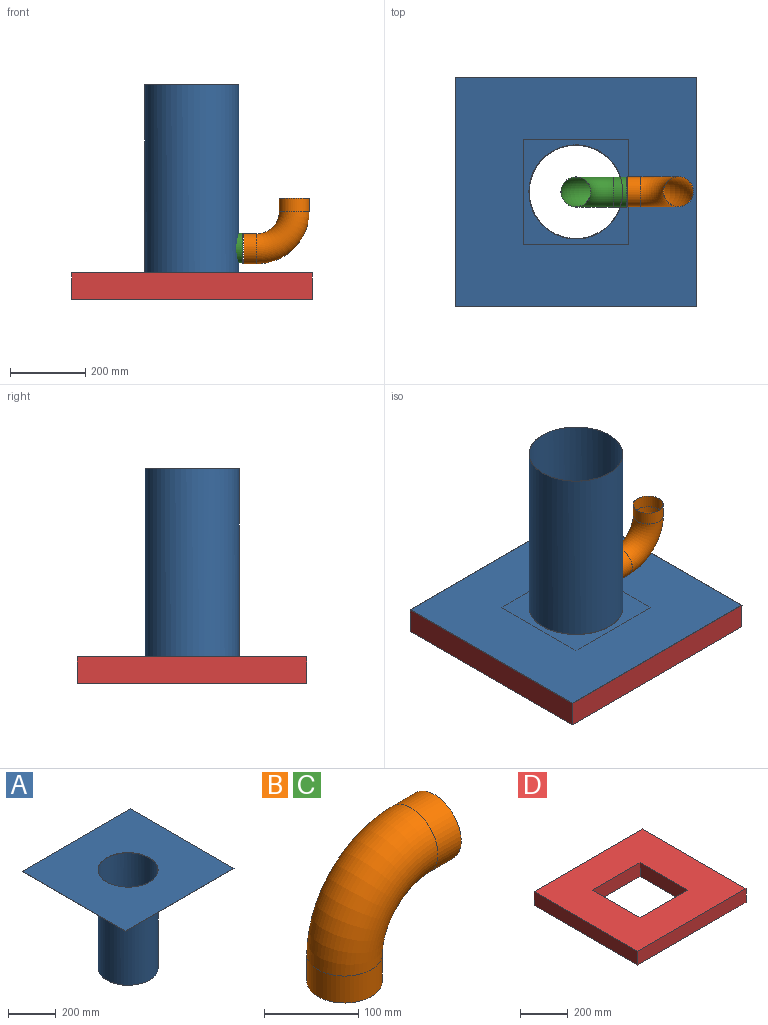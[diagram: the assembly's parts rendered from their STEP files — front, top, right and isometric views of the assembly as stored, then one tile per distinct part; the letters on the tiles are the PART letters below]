
ASSEMBLY  parts=4 mates=2
PART A: 12 faces, bbox 640x610x501 mm
  f0: plane 214.79x210.58mm, normal (0,0,1), area 124.6mm2, adj f1,f2,f8
  f1: cylinder r=124.5mm len=500mm, axis (0,0,-1), area 391128.3mm2, adj f0,f3,f11
  f2: cylinder r=125mm len=500mm, axis (0,0,-1), area 392699.1mm2, adj f0,f3,f4
  f3: plane 250x250mm, normal (0,0,-1), area 391.9mm2, adj f1,f2
  f4: plane 640x610mm, normal (0,0,-1), area 341312.6mm2, adj f2,f5,f6,f7,f8,f9
  f5: plane 610x1mm, normal (-1,0,0), area 610mm2, adj f4,f6,f9,f10
  f6: plane 640x1mm, normal (0,-1,0), area 640mm2, adj f4,f5,f7,f10
  f7: plane 610x1mm, normal (1,0,0), area 610mm2, adj f4,f6,f9,f10
  f8: cylinder r=124.5mm len=249mm, axis (0,0,-1), area 782.3mm2, adj f0,f4,f10,f11
  f9: plane 640x1mm, normal (0,1,0), area 640mm2, adj f4,f5,f7,f10
  f10: plane 640x610mm, normal (0,0,1), area 341704.5mm2, adj f5,f6,f7,f8,f9
  f11: plane 214.79x210.58mm, normal (0,0,-1), area 124.6mm2, adj f1,f8
PART B: 8 faces, bbox 186.5x80x186.5 mm
  f0: torus R=100mm, axis (0,-1,0), area 38984.9mm2, adj f2,f5
  f1: torus R=100mm, axis (0,-1,0), area 39478.4mm2, adj f3,f6
  f2: cylinder r=39.5mm len=79mm, axis (-1,0,0), area 8686.5mm2, adj f0,f4
  f3: cylinder r=40mm len=80mm, axis (-1,0,0), area 8796.5mm2, adj f1,f4
  f4: plane 80x80mm, normal (1,0,0), area 124.9mm2, adj f2,f3
  f5: cylinder r=39.5mm len=79mm, axis (0,0,1), area 8686.5mm2, adj f0,f7
  f6: cylinder r=40mm len=80mm, axis (0,0,1), area 8796.5mm2, adj f1,f7
  f7: plane 80x80mm, normal (0,0,-1), area 124.9mm2, adj f5,f6
PART C: same geometry as B
PART D: 10 faces, bbox 640x610x70 mm
  f0: plane 610x70mm, normal (-1,0,0), area 42700mm2, adj f1,f7,f8,f9
  f1: plane 640x70mm, normal (0,-1,0), area 44800mm2, adj f0,f2,f8,f9
  f2: plane 610x70mm, normal (1,0,0), area 42700mm2, adj f1,f7,f8,f9
  f3: plane 280x70mm, normal (0,1,0), area 19600mm2, adj f4,f6,f8,f9
  f4: plane 280x70mm, normal (1,0,0), area 19600mm2, adj f3,f5,f8,f9
  f5: plane 280x70mm, normal (0,-1,0), area 19600mm2, adj f4,f6,f8,f9
  f6: plane 280x70mm, normal (-1,0,0), area 19600mm2, adj f3,f5,f8,f9
  f7: plane 640x70mm, normal (0,1,0), area 44800mm2, adj f0,f2,f8,f9
  f8: plane 640x610mm, normal (0,0,1), area 312000mm2, adj f0,f1,f2,f3,f4,f5,f6,f7
  f9: plane 640x610mm, normal (0,0,-1), area 312000mm2, adj f0,f1,f2,f3,f4,f5,f6,f7
PLACE A rot(axis=(0,1,0),180deg) t=(-199.14,-74.24,659.28)mm
PLACE B rot(axis=(-0.71,0,-0.71),180deg) t=(31.24,105.56,-192.64)mm
PLACE C rot(axis=(0,-1,0),90deg) t=(98.24,-116.64,-190.73)mm
PLACE D t=(55.99,-73.89,18.28)mm fixed
MATE fastened C.f2 <-> A.f1  axis (0,0,-1) through (-71.76,-6.04,289.28)mm
MATE fastened A.f8 <-> D.f8  axis (0,0,-1) through (-71.39,-5.7,88.28)mm
